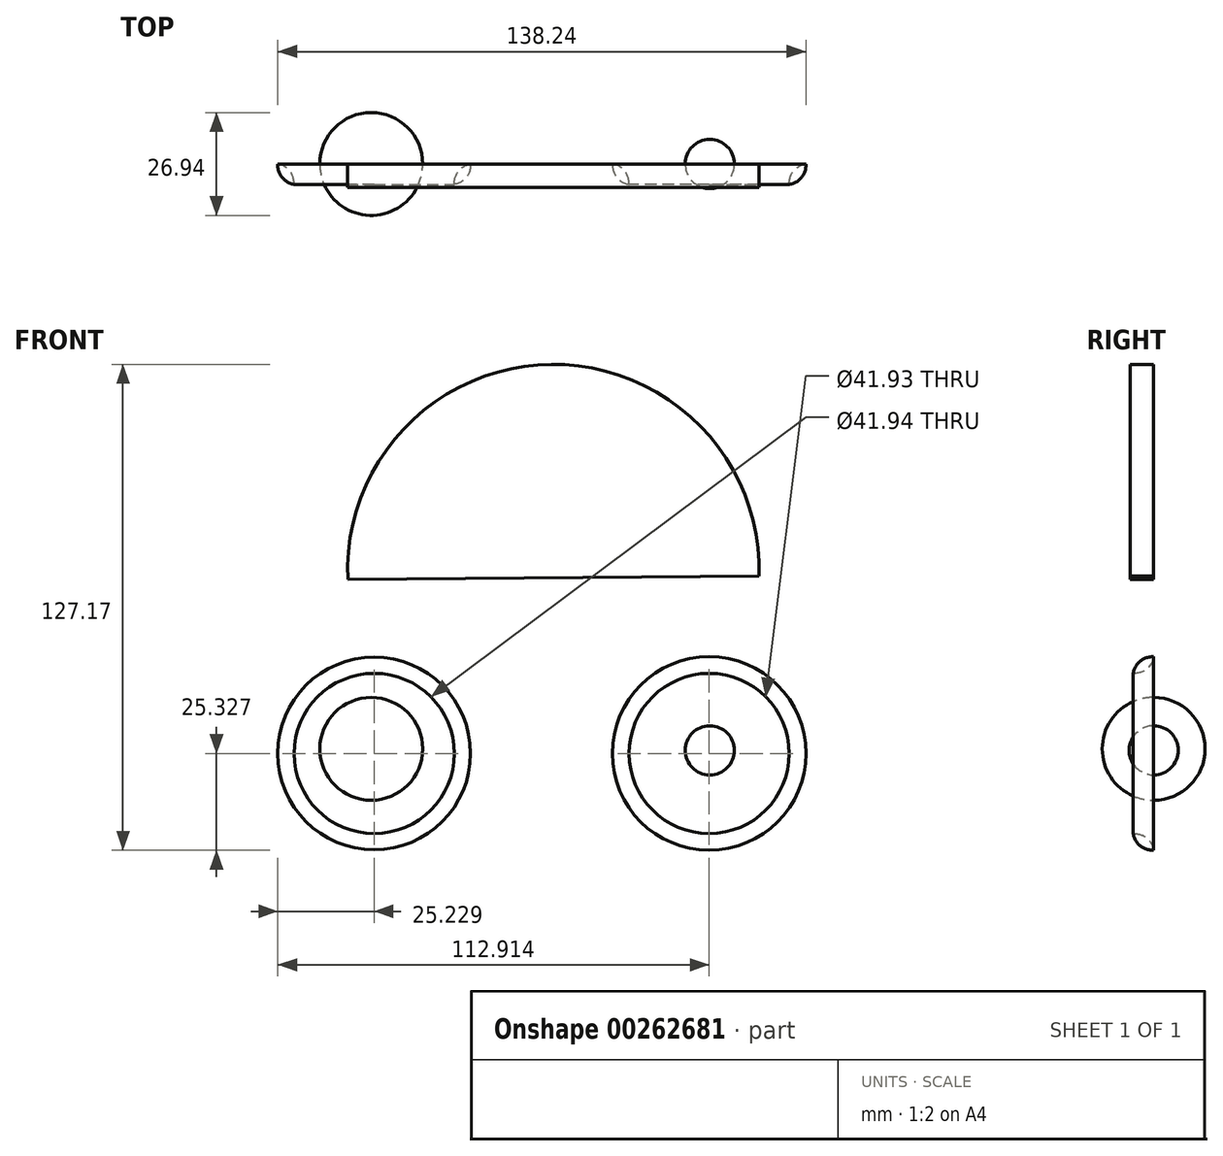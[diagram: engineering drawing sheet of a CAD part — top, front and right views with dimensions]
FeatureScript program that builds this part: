
annotation { "Feature Type Name" : "Feature", "Feature Type Description" : "" }
export const myFeature = defineFeature(function(context is Context, id is Id, definition is map)
    precondition{}
    {
        {
            var Q0;
            Q0=qCreatedBy(makeId("Front.planeOp"),FACE);
            var sketch = newSketch(context, id + "F0", { "sketchPlane" : qUnion([Q0])});
            skCircle(sketch, "E0", {"center": v(-49.31, -28.01) * mm, "radius": 25.23 * mm});
            skCircle(sketch, "E1", {"center": v(38.37, -28.01) * mm, "radius": 25.33 * mm});
            skCircle(sketch, "E2", {"center": v(-49.31, -28.01) * mm, "radius": 20.97 * mm});
            skCircle(sketch, "E3", {"center": v(38.37, -28.01) * mm, "radius": 20.97 * mm});
            skSolve(sketch);
        }
        {
            var Q0;
            Q0=makeQuery(id+"F0.imprint","IMPRINT",FACE,{"disambiguationData":[TD([[makeQuery(id+"F0.imprint","IMPRINT",EDGE,{"derivedFrom":sQuery(id+"F0.wireOp",EDGE,"E1")}),1.0]])]});
            var Q1;
            Q1=makeQuery(id+"F0.imprint","IMPRINT",FACE,{"disambiguationData":[TD([[makeQuery(id+"F0.imprint","IMPRINT",EDGE,{"derivedFrom":sQuery(id+"F0.wireOp",EDGE,"E0")}),1.0]])]});
            extrude(context, id + "F1", {"entities" : qUnion([Q0, Q1]), "depth" : 5.33 * mm});
        }
        {
            var Q0;
            Q0=makeQuery(id+"F1.opExtrude","CAP_EDGE",EDGE,{"disambiguationData":[OSD([sQuery(id+"F0.wireOp",EDGE,"E0")])],"isStart":false});
            var Q1;
            Q1=makeQuery(id+"F1.opExtrude","CAP_EDGE",EDGE,{"disambiguationData":[OSD([sQuery(id+"F0.wireOp",EDGE,"E1")])],"isStart":false});
            fillet(context, id + "F2", {"entities" : qUnion([Q0, Q1]), "radius" : 5.08 * mm, "tangentPropagation" : true, "allowEdgeOverflow" : false});
        }
        {
            var Q0;
            Q0=makeQuery(id+"F1.opExtrude","CAP_EDGE",EDGE,{"disambiguationData":[OSD([sQuery(id+"F0.wireOp",EDGE,"E3")])],"isStart":true});
            var Q1;
            Q1=makeQuery(id+"F1.opExtrude","CAP_EDGE",EDGE,{"disambiguationData":[OSD([sQuery(id+"F0.wireOp",EDGE,"E2")])],"isStart":true});
            fillet(context, id + "F3", {"entities" : qUnion([Q0, Q1]), "radius" : 5.08 * mm, "tangentPropagation" : true, "allowEdgeOverflow" : false});
        }
        {
            var Q0;
            Q0=qCreatedBy(makeId("Front.planeOp"),FACE);
            var sketch = newSketch(context, id + "F4", { "sketchPlane" : qUnion([Q0])});
            skCircle(sketch, "E4", {"center": v(38.54, -27.2) * mm, "radius": 6.43 * mm});
            skLineSegment(sketch, "E5", {"start": v(38.54, -20.76) * mm, "end": v(38.54, -33.62) * mm});
            skSolve(sketch);
        }
        {
            var Q0;
            {var subQ0=sQuery(id+"F4.wireOp",EDGE,"E5");Q0=makeQuery(id+"F4.imprint","IMPRINT",FACE,{"disambiguationData":[TD([[makeQuery(id+"F4.imprint","IMPRINT",EDGE,{"derivedFrom":subQ0}),1.0]])]});}
            var Q1;
            Q1=sQuery(id+"F4.wireOp",EDGE,"E5");
            revolve(context, id + "F5", {"entities" : qUnion([Q0]), "axis" : qUnion([Q1]), "revolveType" : RevolveType.FULL});
        }
        {
            var Q0;
            Q0=qCreatedBy(makeId("Front.planeOp"),FACE);
            var sketch = newSketch(context, id + "F6", { "sketchPlane" : qUnion([Q0])});
            skCircle(sketch, "E6", {"center": v(-50.07, -26.8) * mm, "radius": 13.47 * mm});
            skLineSegment(sketch, "E7", {"start": v(-50.07, -13.34) * mm, "end": v(-50.07, -40.27) * mm});
            skSolve(sketch);
        }
        {
            var Q0;
            {var subQ0=sQuery(id+"F6.wireOp",EDGE,"E7");Q0=makeQuery(id+"F6.imprint","IMPRINT",FACE,{"disambiguationData":[TD([[makeQuery(id+"F6.imprint","IMPRINT",EDGE,{"derivedFrom":subQ0}),1.0]])]});}
            var Q1;
            Q1=sQuery(id+"F6.wireOp",EDGE,"E7");
            revolve(context, id + "F7", {"entities" : qUnion([Q0]), "axis" : qUnion([Q1]), "revolveType" : RevolveType.FULL});
        }
        {
            var Q0;
            Q0=qCreatedBy(makeId("Front.planeOp"),FACE);
            var sketch = newSketch(context, id + "F8", { "sketchPlane" : qUnion([Q0])});
            skArc(sketch, "E8", {"start": v(51.43, 18.47) * mm, "mid": v(-2.88, 73.83) * mm, "end": v(-56.2, 17.51) * mm});
            skLineSegment(sketch, "E9", {"start": v(51.43, 18.47) * mm, "end": v(-56.2, 17.51) * mm});
            skLineSegment(sketch, "E10", {"start": v(-2.39, 18) * mm, "end": v(-2.39, 73.83) * mm});
            skSolve(sketch);
        }
        {
            var Q0;
            {var subQ3=sQuery(id+"F8.wireOp",EDGE,"E10");Q0=makeQuery(id+"F8.imprint","IMPRINT",FACE,{"disambiguationData":[TD([[makeQuery(id+"F8.imprint","IMPRINT",EDGE,{"derivedFrom":subQ3}),1.0]])]});}
            var Q1;
            {var subQ3=sQuery(id+"F8.wireOp",EDGE,"E10");Q1=makeQuery(id+"F8.imprint","IMPRINT",FACE,{"disambiguationData":[TD([[makeQuery(id+"F8.imprint","IMPRINT",EDGE,{"derivedFrom":subQ3}),-1.0]])]});}
            extrude(context, id + "F9", {"entities" : qUnion([Q0, Q1]), "depth" : 6.1 * mm});
        }
    });
